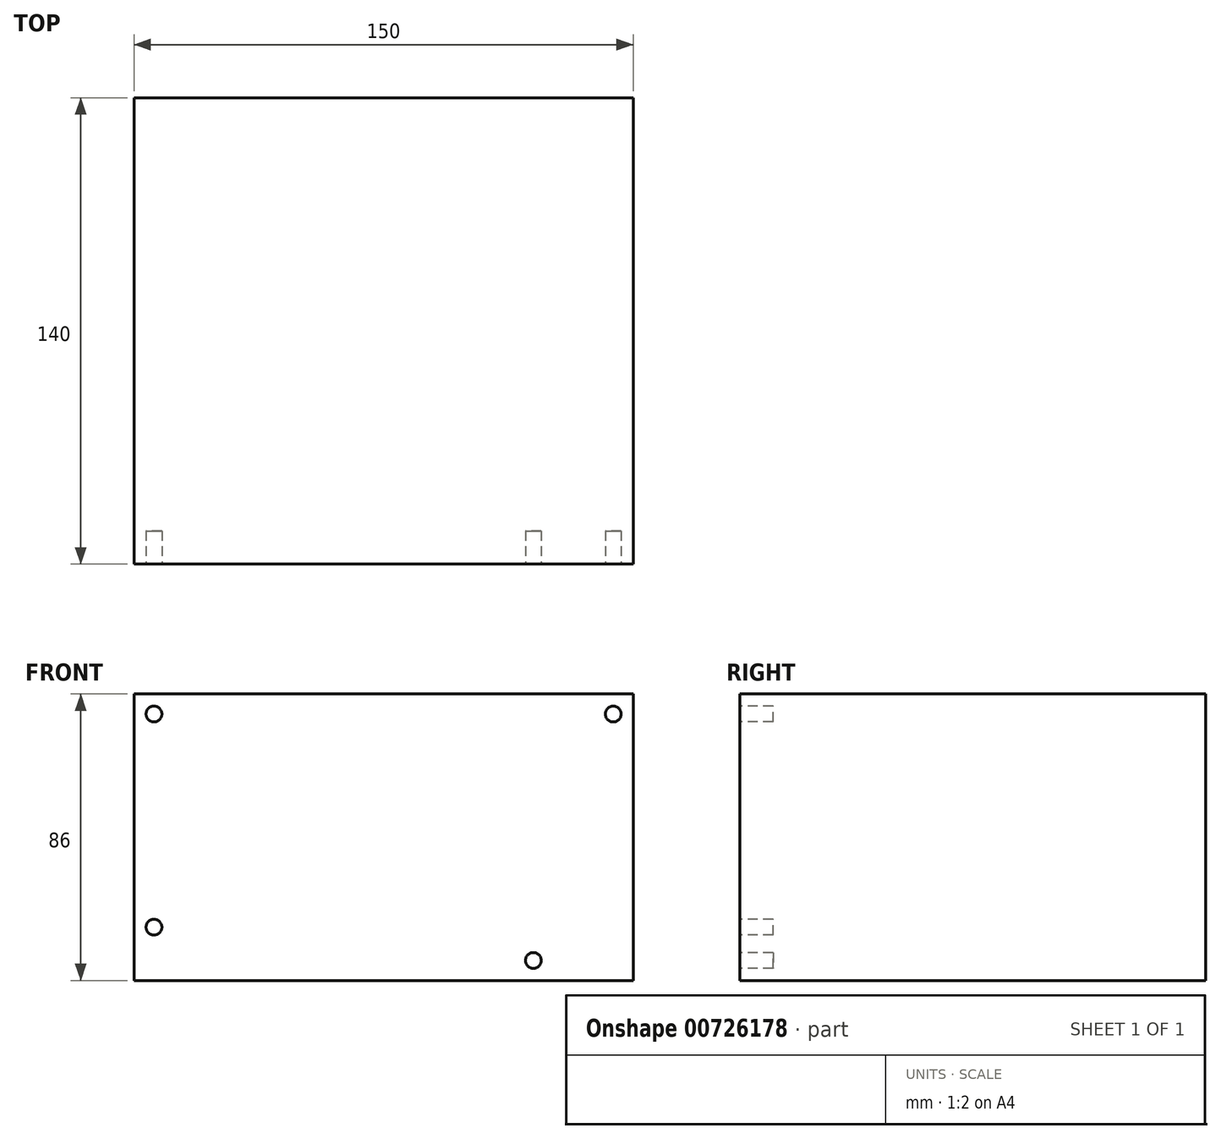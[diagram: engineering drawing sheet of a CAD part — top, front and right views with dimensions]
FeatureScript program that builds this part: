
annotation { "Feature Type Name" : "Feature", "Feature Type Description" : "" }
export const myFeature = defineFeature(function(context is Context, id is Id, definition is map)
    precondition{}
    {
        {
            var Q0;
            Q0=qCreatedBy(makeId("Top.planeOp"),FACE);
            var sketch = newSketch(context, id + "F0", { "sketchPlane" : qUnion([Q0])});
            skLineSegment(sketch, "E0.bottom", {"start": v(75, -70) * mm, "end": v(-75, -70) * mm});
            skLineSegment(sketch, "E0.top", {"start": v(75, 70) * mm, "end": v(-75, 70) * mm});
            skLineSegment(sketch, "E0.left", {"start": v(75, -70) * mm, "end": v(75, 70) * mm});
            skLineSegment(sketch, "E0.right", {"start": v(-75, -70) * mm, "end": v(-75, 70) * mm});
            skPoint(sketch, "E0.middle", {"position": v(0, 0) * mm});
            skSolve(sketch);
        }
        {
            var Q0;
            Q0=makeQuery(id+"F0.imprint","IMPRINT",FACE,{"disambiguationData":[TD([[makeQuery(id+"F0.imprint","IMPRINT",EDGE,{"derivedFrom":sQuery(id+"F0.wireOp",EDGE,"E0.bottom")}),-1.0]])]});
            extrude(context, id + "F1", {"entities" : qUnion([Q0]), "depth" : 86 * mm, "offsetDistance" : 25 * mm});
        }
        {
            var Q0;
            Q0=makeQuery(id+"F1.opExtrude","SWEPT_FACE",FACE,{"disambiguationData":[OSD([sQuery(id+"F0.wireOp",EDGE,"E0.bottom")])]});
            var sketch = newSketch(context, id + "F2", { "sketchPlane" : qUnion([Q0])});
            skCircle(sketch, "E1", {"center": v(-69, 80) * mm, "radius": 2.38 * mm});
            skCircle(sketch, "E2", {"center": v(-69, 16) * mm, "radius": 2.38 * mm});
            skLineSegment(sketch, "E3", {"start": v(-69, 80) * mm, "end": v(-69, 16) * mm, "construction": true});
            skCircle(sketch, "E4", {"center": v(69, 80) * mm, "radius": 2.38 * mm});
            skCircle(sketch, "E5", {"center": v(45, 6) * mm, "radius": 2.38 * mm});
            skSolve(sketch);
        }
        {
            var Q0;
            Q0 = qSketchRegion(id + "F2", true);
            extrude(context, id + "F3", {"entities" : qUnion([Q0]), "operationType" : NewBodyOperationType.REMOVE, "oppositeDirection" : true, "depth" : 10 * mm, "offsetDistance" : 25 * mm});
        }
    });
